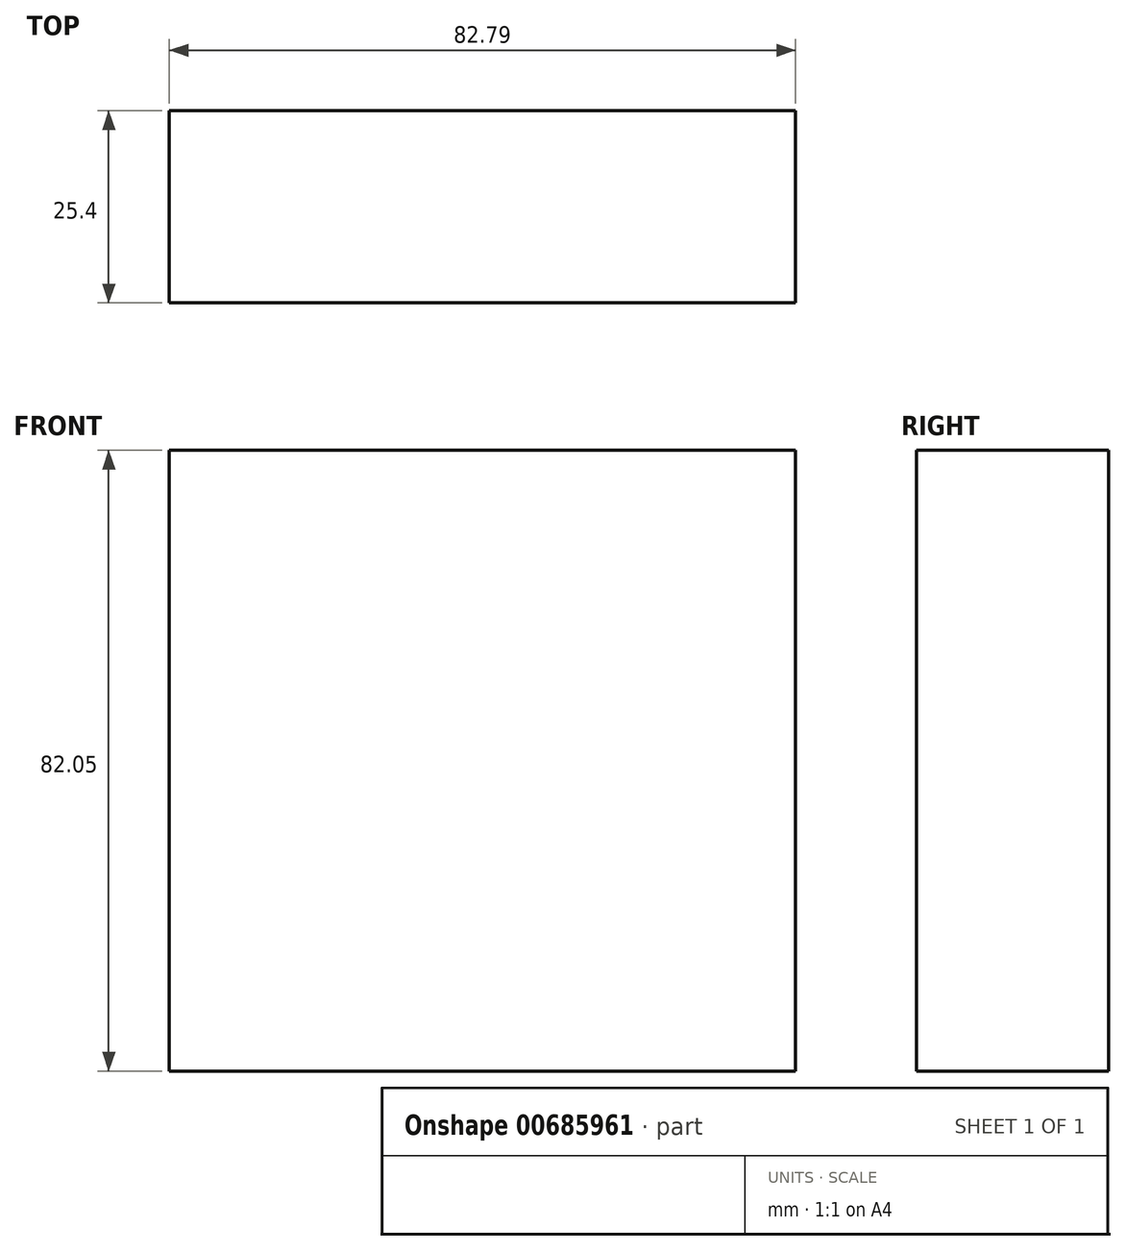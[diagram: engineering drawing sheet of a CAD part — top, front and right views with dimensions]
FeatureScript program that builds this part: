
annotation { "Feature Type Name" : "Feature", "Feature Type Description" : "" }
export const myFeature = defineFeature(function(context is Context, id is Id, definition is map)
    precondition{}
    {
        {
            var Q0;
            Q0=qCreatedBy(makeId("Front.planeOp"),FACE);
            var sketch = newSketch(context, id + "F0", { "sketchPlane" : qUnion([Q0])});
            skLineSegment(sketch, "E0.bottom", {"start": v(-41.95, 50.77) * mm, "end": v(40.84, 50.77) * mm});
            skLineSegment(sketch, "E0.top", {"start": v(-41.95, -31.28) * mm, "end": v(40.84, -31.28) * mm});
            skLineSegment(sketch, "E0.left", {"start": v(-41.95, 50.77) * mm, "end": v(-41.95, -31.28) * mm});
            skLineSegment(sketch, "E0.right", {"start": v(40.84, 50.77) * mm, "end": v(40.84, -31.28) * mm});
            skSolve(sketch);
        }
        {
            var Q0;
            Q0=makeQuery(id+"F0.imprint","IMPRINT",FACE,{"disambiguationData":[TD([[makeQuery(id+"F0.imprint","IMPRINT",EDGE,{"derivedFrom":sQuery(id+"F0.wireOp",EDGE,"E0.bottom")}),-1.0]])]});
            extrude(context, id + "F1", {"entities" : qUnion([Q0]), "depth" : 25.4 * mm, "offsetDistance" : 25.4 * mm});
        }
    });
